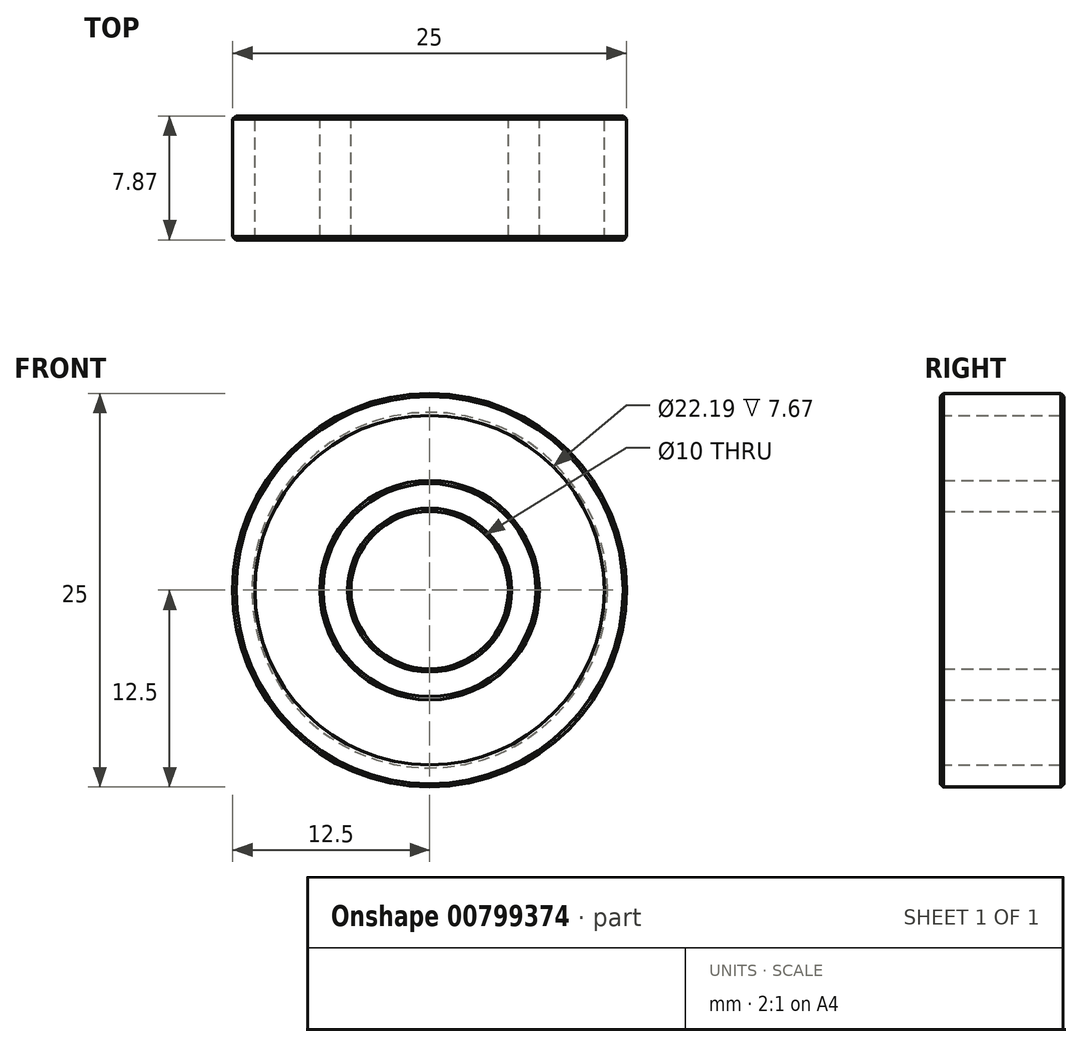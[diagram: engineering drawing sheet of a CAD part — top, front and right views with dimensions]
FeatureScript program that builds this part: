
annotation { "Feature Type Name" : "Feature", "Feature Type Description" : "" }
export const myFeature = defineFeature(function(context is Context, id is Id, definition is map)
    precondition{}
    {
        {
            var Q0;
            Q0=qCreatedBy(makeId("Front.planeOp"),FACE);
            var sketch = newSketch(context, id + "F0", { "sketchPlane" : qUnion([Q0])});
            skCircle(sketch, "E0", {"center": v(0, 0) * mm, "radius": 12.5 * mm});
            skCircle(sketch, "E1", {"center": v(0, 0) * mm, "radius": 11.1 * mm});
            skCircle(sketch, "E2", {"center": v(0, 0) * mm, "radius": 6.96 * mm});
            skCircle(sketch, "E3", {"center": v(0, 0) * mm, "radius": 5 * mm});
            skSolve(sketch);
        }
        {
            var Q0;
            Q0=makeQuery(id+"F0.imprint","IMPRINT",FACE,{"disambiguationData":[TD([[makeQuery(id+"F0.imprint","IMPRINT",EDGE,{"derivedFrom":sQuery(id+"F0.wireOp",EDGE,"E0")}),1.0]])]});
            var Q1;
            Q1=makeQuery(id+"F0.imprint","IMPRINT",FACE,{"disambiguationData":[TD([[makeQuery(id+"F0.imprint","IMPRINT",EDGE,{"derivedFrom":sQuery(id+"F0.wireOp",EDGE,"E2")}),1.0]])]});
            extrude(context, id + "F1", {"entities" : qUnion([Q0, Q1]), "depth" : 7.87 * mm, "offsetDistance" : 25 * mm});
        }
        {
            var Q0;
            Q0=makeQuery(id+"F1.opExtrude","CAP_EDGE",EDGE,{"disambiguationData":[OSD([sQuery(id+"F0.wireOp",EDGE,"E3")])],"isStart":false});
            chamfer(context, id + "F2", {"entities" : qUnion([Q0]), "width" : .2 * mm, "tangentPropagation" : true});
        }
        {
            var Q0;
            Q0=makeQuery(id+"F1.opExtrude","CAP_EDGE",EDGE,{"disambiguationData":[OSD([sQuery(id+"F0.wireOp",EDGE,"E3")])],"isStart":true});
            chamfer(context, id + "F3", {"entities" : qUnion([Q0]), "width" : 0.2 * mm, "tangentPropagation" : true});
        }
        {
            var Q0;
            Q0=makeQuery(id+"F1.opExtrude","CAP_EDGE",EDGE,{"disambiguationData":[OSD([sQuery(id+"F0.wireOp",EDGE,"E0")])],"isStart":false});
            var Q1;
            Q1=makeQuery(id+"F1.opExtrude","CAP_EDGE",EDGE,{"disambiguationData":[OSD([sQuery(id+"F0.wireOp",EDGE,"E0")])],"isStart":true});
            chamfer(context, id + "F4", {"entities" : qUnion([Q0, Q1]), "width" : 0.2 * mm, "tangentPropagation" : true});
        }
        {
            var Q0;
            Q0=makeQuery(id+"F1.opExtrude","CAP_EDGE",EDGE,{"disambiguationData":[OSD([sQuery(id+"F0.wireOp",EDGE,"E1")])],"isStart":true});
            var Q1;
            Q1=makeQuery(id+"F1.opExtrude","CAP_EDGE",EDGE,{"disambiguationData":[OSD([sQuery(id+"F0.wireOp",EDGE,"E2")])],"isStart":true});
            chamfer(context, id + "F5", {"entities" : qUnion([Q0, Q1]), "width" : 0.2 * mm, "tangentPropagation" : true});
        }
        {
            var Q0;
            Q0=makeQuery(id+"F1.opExtrude","CAP_EDGE",EDGE,{"disambiguationData":[OSD([sQuery(id+"F0.wireOp",EDGE,"E2")])],"isStart":false});
            chamfer(context, id + "F6", {"entities" : qUnion([Q0]), "width" : 0.2 * mm, "tangentPropagation" : true});
        }
    });
